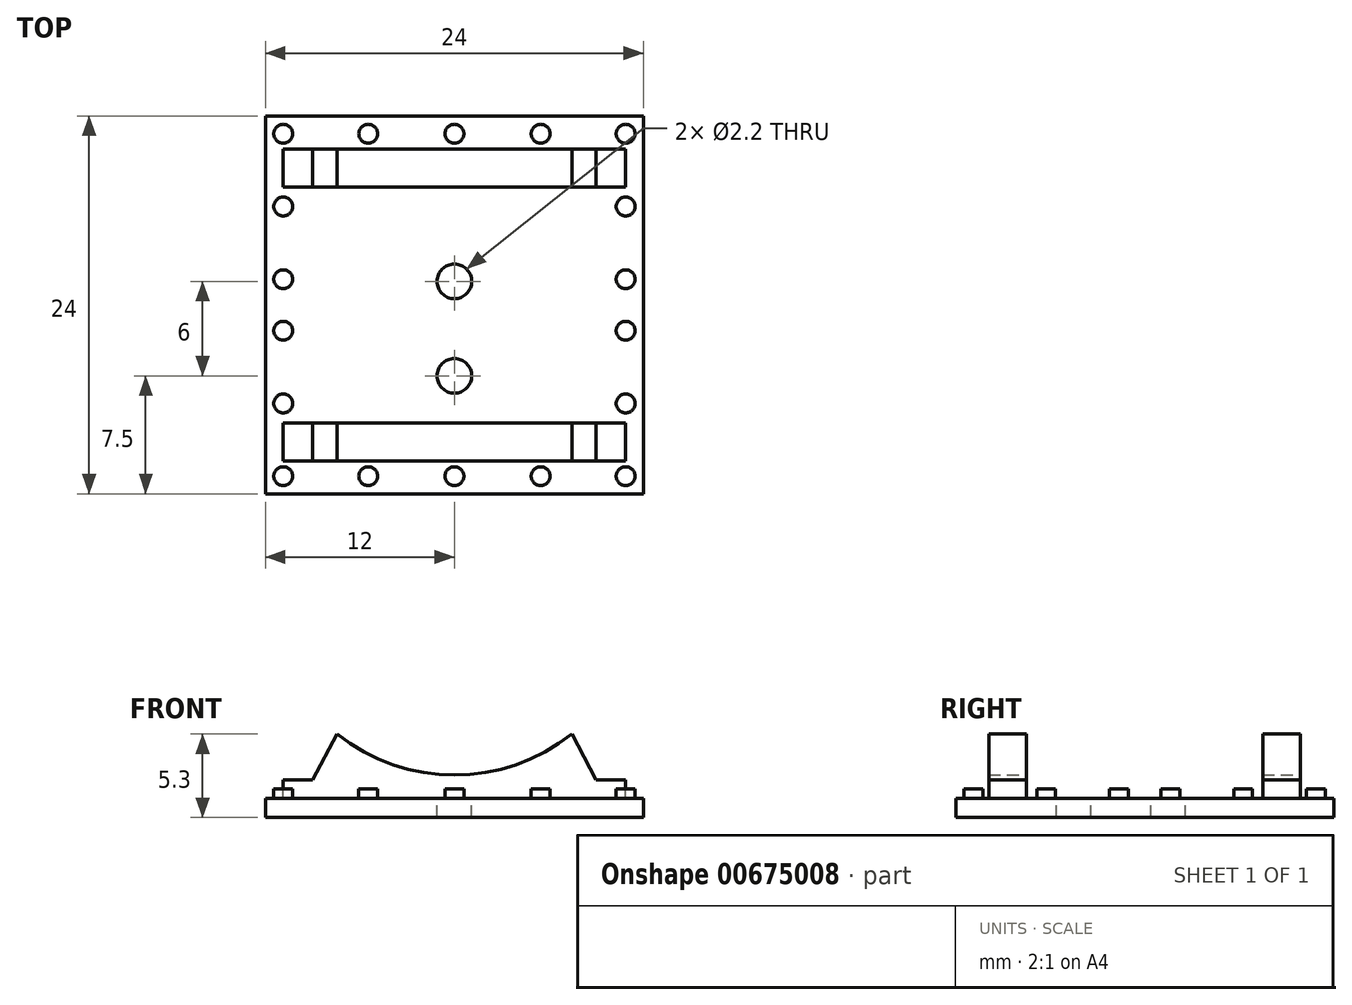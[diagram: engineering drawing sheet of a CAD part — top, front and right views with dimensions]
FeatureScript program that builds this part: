
annotation { "Feature Type Name" : "Feature", "Feature Type Description" : "" }
export const myFeature = defineFeature(function(context is Context, id is Id, definition is map)
    precondition{}
    {
        {
            assignVariable(context, id + "F0", {"name" : "Faktor", "anyValue" : 1.5});
        }
        {
            var Q0;
            Q0=qCreatedBy(makeId("Top.planeOp"),FACE);
            var sketch = newSketch(context, id + "F1", { "sketchPlane" : qUnion([Q0])});
            skLineSegment(sketch, "E0.bottom", {"start": v(-12, -12) * mm, "end": v(12, -12) * mm});
            skLineSegment(sketch, "E0.top", {"start": v(-12, 12) * mm, "end": v(12, 12) * mm});
            skLineSegment(sketch, "E0.left", {"start": v(-12, -12) * mm, "end": v(-12, 12) * mm});
            skLineSegment(sketch, "E0.right", {"start": v(12, -12) * mm, "end": v(12, 12) * mm});
            skPoint(sketch, "E0.middle", {"position": v(0, 0) * mm});
            skSolve(sketch);
        }
        {
            var Q0;
            Q0=qSketchRegion(id+"F1",true);
            extrude(context, id + "F2", {"entities" : qUnion([Q0]), "depth" : getVariable(context, 'Faktor') * 0.8 * mm, "offsetDistance" : 25 * mm});
        }
        {
            var Q0;
            Q0=makeQuery(id+"F2.opExtrude","CAP_FACE",FACE,{"disambiguationData":[OSD([sQuery(id+"F1.wireOp",EDGE,"E0.bottom"),sQuery(id+"F1.wireOp",EDGE,"E0.top"),sQuery(id+"F1.wireOp",EDGE,"E0.left"),sQuery(id+"F1.wireOp",EDGE,"E0.right")])],"isStart":false});
            var sketch = newSketch(context, id + "F3", { "sketchPlane" : qUnion([Q0])});
            skLineSegment(sketch, "E1.bottom", {"start": v(-10.88, 10.88) * mm, "end": v(10.87, 10.88) * mm, "construction": true});
            skLineSegment(sketch, "E1.top", {"start": v(-10.87, -10.88) * mm, "end": v(10.88, -10.88) * mm, "construction": true});
            skLineSegment(sketch, "E1.left", {"start": v(-10.88, 10.88) * mm, "end": v(-10.88, -10.88) * mm, "construction": true});
            skLineSegment(sketch, "E1.right", {"start": v(10.88, 10.88) * mm, "end": v(10.88, -10.88) * mm, "construction": true});
            skPoint(sketch, "E1.middle", {"position": v(0, 0) * mm});
            skCircle(sketch, "E2", {"center": v(-10.88, 10.88) * mm, "radius": 0.6 * mm});
            skCircle(sketch, "E3", {"center": v(-10.88, 6.26) * mm, "radius": 0.6 * mm});
            skCircle(sketch, "E4", {"center": v(-10.88, 1.64) * mm, "radius": 0.6 * mm});
            skCircle(sketch, "E5", {"center": v(-10.88, -1.64) * mm, "radius": 0.6 * mm});
            skCircle(sketch, "E6", {"center": v(-10.88, -6.26) * mm, "radius": 0.6 * mm});
            skCircle(sketch, "E7", {"center": v(-10.87, -10.88) * mm, "radius": 0.6 * mm});
            skCircle(sketch, "E8", {"center": v(-5.48, 10.88) * mm, "radius": 0.6 * mm});
            skCircle(sketch, "E9", {"center": v(0, 10.88) * mm, "radius": 0.6 * mm});
            skCircle(sketch, "E10", {"center": v(5.47, 10.88) * mm, "radius": 0.6 * mm});
            skCircle(sketch, "E11", {"center": v(10.87, 10.88) * mm, "radius": 0.6 * mm});
            skCircle(sketch, "E12", {"center": v(10.88, 6.26) * mm, "radius": 0.6 * mm});
            skCircle(sketch, "E13", {"center": v(10.88, 1.64) * mm, "radius": 0.6 * mm});
            skCircle(sketch, "E14", {"center": v(10.88, -1.64) * mm, "radius": 0.6 * mm});
            skCircle(sketch, "E15", {"center": v(10.88, -6.26) * mm, "radius": 0.6 * mm});
            skCircle(sketch, "E16", {"center": v(10.88, -10.88) * mm, "radius": 0.6 * mm});
            skCircle(sketch, "E17", {"center": v(0, -10.88) * mm, "radius": 0.6 * mm});
            skCircle(sketch, "E18", {"center": v(5.48, -10.88) * mm, "radius": 0.6 * mm});
            skCircle(sketch, "E19", {"center": v(-5.47, -10.88) * mm, "radius": 0.6 * mm});
            skSolve(sketch);
        }
        {
            var Q0;
            Q0=qSketchRegion(id+"F3",true);
            extrude(context, id + "F4", {"entities" : qUnion([Q0]), "operationType" : NewBodyOperationType.ADD, "depth" : 0.6 * mm, "offsetDistance" : 25 * mm});
        }
        {
            var Q0;
            Q0=qCreatedBy(makeId("Front.planeOp"),FACE);
            cPlane(context, id + "F5", {"entities" : qUnion([Q0]), "cplaneType" : CPlaneType.OFFSET, "offset" : getVariable(context, 'Faktor') * 5 * mm, "width" : 150 * mm, "height" : 150 * mm});
        }
        {
            var Q0;
            Q0=qCreatedBy(id+"F5.planeOp",FACE);
            var sketch = newSketch(context, id + "F6", { "sketchPlane" : qUnion([Q0])});
            skArc(sketch, "E20", {"start": v(-6.75, 6.66) * mm, "mid": v(0, 4.2) * mm, "end": v(6.75, 6.66) * mm});
            skLineSegment(sketch, "E21.0", {"start": v(-12, 1.2) * mm, "end": v(12, 1.2) * mm, "construction": true});
            skLineSegment(sketch, "E22.bottom", {"start": v(-10.88, 1.2) * mm, "end": v(10.88, 1.2) * mm});
            skLineSegment(sketch, "E22.top", {"start": v(-10.88, 2.4) * mm, "end": v(-9, 2.4) * mm});
            skLineSegment(sketch, "E22.left", {"start": v(-10.88, 1.2) * mm, "end": v(-10.88, 2.4) * mm});
            skLineSegment(sketch, "E22.right", {"start": v(10.88, 1.2) * mm, "end": v(10.88, 2.4) * mm});
            skLineSegment(sketch, "E23", {"start": v(-9, 2.4) * mm, "end": v(-6.75, 6.66) * mm});
            skLineSegment(sketch, "E24", {"start": v(6.75, 6.66) * mm, "end": v(9, 2.4) * mm});
            skLineSegment(sketch, "E25.trimOffspring", {"start": v(9, 2.4) * mm, "end": v(10.88, 2.4) * mm});
            skSolve(sketch);
        }
        {
            var Q0;
            Q0=qSketchRegion(id+"F6",true);
            extrude(context, id + "F7", {"entities" : qUnion([Q0]), "depth" : getVariable(context, 'Faktor') * 1.6 * mm, "offsetDistance" : 25 * mm});
        }
        {
            var Q0;
            Q0=makeQuery(id+"F7.opExtrude","SWEPT_BODY",BODY,{"disambiguationData":[OSD([sQuery(id+"F6.wireOp",EDGE,"E20"),sQuery(id+"F6.wireOp",EDGE,"E22.bottom"),sQuery(id+"F6.wireOp",EDGE,"E22.top"),sQuery(id+"F6.wireOp",EDGE,"E22.left"),sQuery(id+"F6.wireOp",EDGE,"E22.right"),sQuery(id+"F6.wireOp",EDGE,"E23"),sQuery(id+"F6.wireOp",EDGE,"E24"),sQuery(id+"F6.wireOp",EDGE,"E25.trimOffspring")])]});
            var Q1;
            Q1=qCreatedBy(makeId("Front.planeOp"),FACE);
            mirror(context, id + "F8", {"operationType" : NewBodyOperationType.ADD, "entities" : qUnion([Q0]), "mirrorPlane" : qUnion([Q1])});
        }
        {
            var Q0;
            Q0=qCreatedBy(id+"F5.planeOp",FACE);
            var sketch = newSketch(context, id + "F9", { "sketchPlane" : qUnion([Q0])});
            skArc(sketch, "E26.0", {"start": v(-6.75, 6.66) * mm, "mid": v(0, 4.2) * mm, "end": v(6.75, 6.66) * mm, "construction": true});
            skCircle(sketch, "E27", {"center": v(0, 14.7) * mm, "radius": 12 * mm});
            skSolve(sketch);
        }
        {
            var Q0;
            Q0=qSketchRegion(id+"F9",true);
            extrude(context, id + "F10", {"entities" : qUnion([Q0]), "operationType" : NewBodyOperationType.REMOVE, "endBound" : BoundingType.SYMMETRIC, "depth" : getVariable(context, 'Faktor') * 25 * mm, "offsetDistance" : 25 * mm});
        }
        {
            var Q0;
            Q0=makeQuery(id+"F2.opExtrude","CAP_FACE",FACE,{"disambiguationData":[OSD([sQuery(id+"F1.wireOp",EDGE,"E0.bottom"),sQuery(id+"F1.wireOp",EDGE,"E0.top"),sQuery(id+"F1.wireOp",EDGE,"E0.left"),sQuery(id+"F1.wireOp",EDGE,"E0.right")])],"isStart":false});
            var sketch = newSketch(context, id + "F11", { "sketchPlane" : qUnion([Q0])});
            skCircle(sketch, "E28", {"center": v(0, -4.5) * mm, "radius": 1.1 * mm});
            skCircle(sketch, "E29", {"center": v(0, 1.5) * mm, "radius": 1.1 * mm});
            skSolve(sketch);
        }
        {
            var Q0;
            Q0=qSketchRegion(id+"F11",true);
            extrude(context, id + "F12", {"entities" : qUnion([Q0]), "operationType" : NewBodyOperationType.REMOVE, "endBound" : BoundingType.THROUGH_ALL, "oppositeDirection" : true, "depth" : 25 * mm, "offsetDistance" : 25 * mm});
        }
    });
